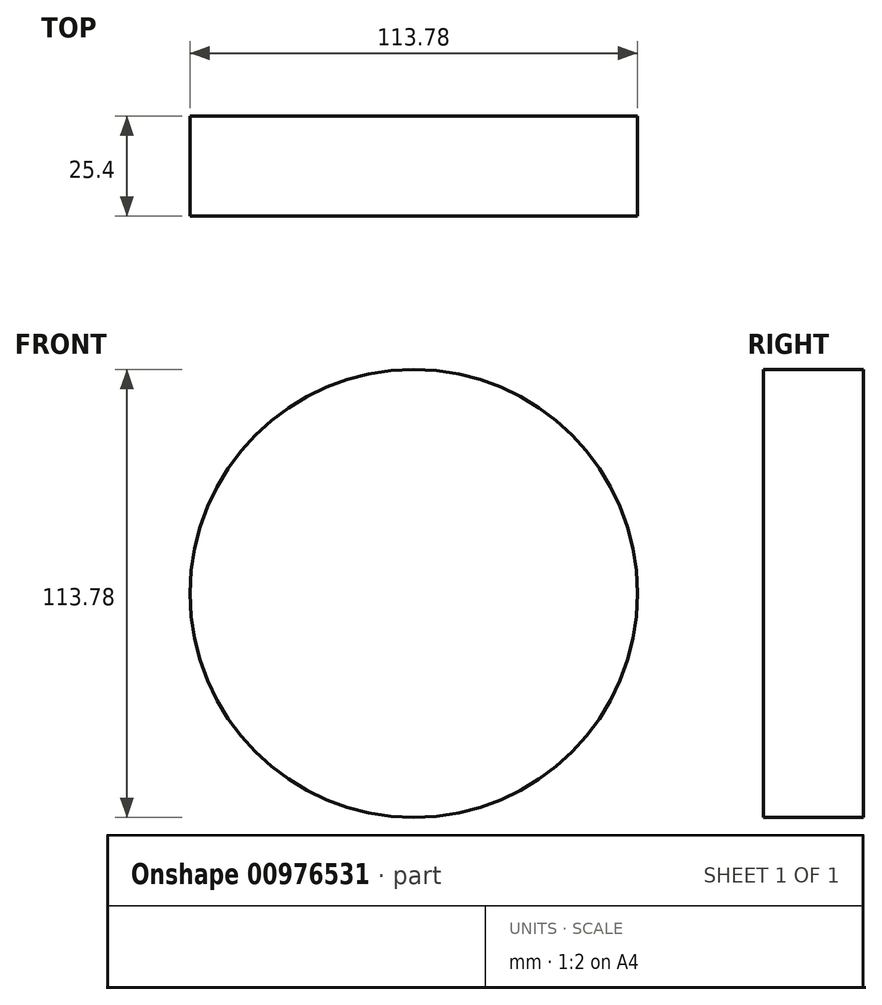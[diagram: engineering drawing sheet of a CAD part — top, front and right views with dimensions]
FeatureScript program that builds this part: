
annotation { "Feature Type Name" : "Feature", "Feature Type Description" : "" }
export const myFeature = defineFeature(function(context is Context, id is Id, definition is map)
    precondition{}
    {
        {
            var Q0;
            Q0=qCreatedBy(makeId("Front.planeOp"),FACE);
            var sketch = newSketch(context, id + "F0", { "sketchPlane" : qUnion([Q0])});
            skPoint(sketch, "E0.start.orphan", {"position": v(-38.55, 43.87) * mm});
            skPoint(sketch, "E1.start.orphan", {"position": v(-55.26, 43.87) * mm});
            skPoint(sketch, "E2.end.orphan", {"position": v(-35.51, 24.5) * mm});
            skPoint(sketch, "E2.start.orphan", {"position": v(-55.26, 24.5) * mm});
            skPoint(sketch, "E3.MirrorCS.end.orphan", {"position": v(-16.52, 24.5) * mm});
            skPoint(sketch, "E4.MirrorCS.end.orphan", {"position": v(3.23, 24.5) * mm});
            skPoint(sketch, "E5.MirrorCS.end.orphan", {"position": v(3.23, 43.87) * mm});
            skPoint(sketch, "E5.MirrorCS.start.orphan", {"position": v(-13.48, 43.87) * mm});
            skPoint(sketch, "E6.trimOffspring.end.orphan", {"position": v(-5.13, 0) * mm});
            skCircle(sketch, "E7", {"center": v(-16.52, 9.9) * mm, "radius": 56.89 * mm});
            skSolve(sketch);
        }
        {
            var Q0;
            Q0=makeQuery(id+"F0.imprint","IMPRINT",FACE,{"disambiguationData":[TD([[makeQuery(id+"F0.imprint","IMPRINT",EDGE,{"derivedFrom":sQuery(id+"F0.wireOp",EDGE,"E7")}),1.0]])]});
            extrude(context, id + "F1", {"entities" : qUnion([Q0]), "depth" : 25.4 * mm, "offsetDistance" : 25.4 * mm});
        }
    });
